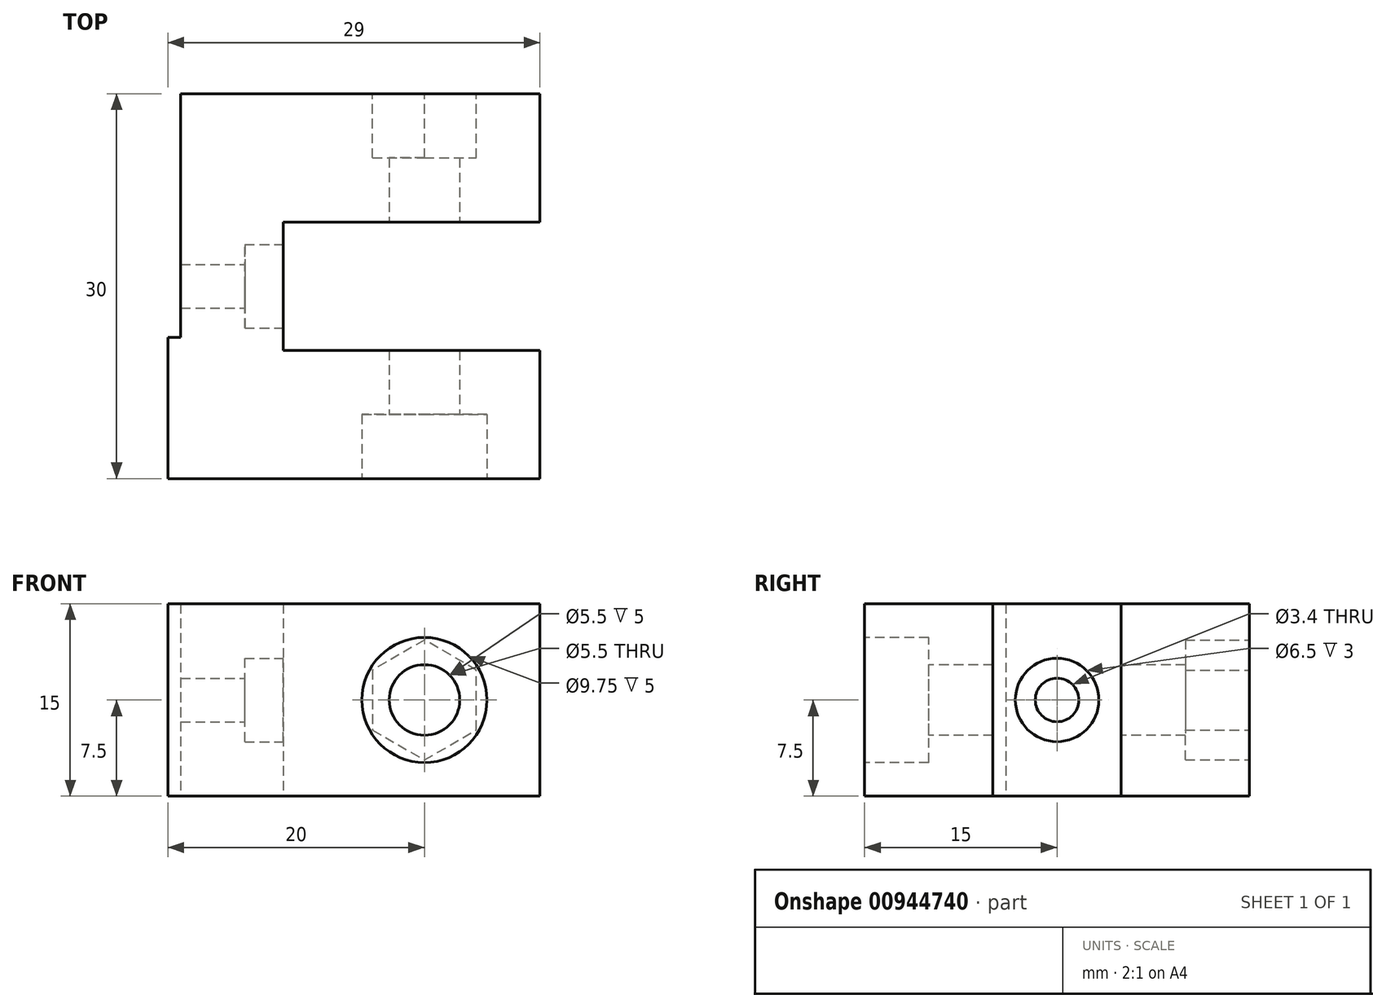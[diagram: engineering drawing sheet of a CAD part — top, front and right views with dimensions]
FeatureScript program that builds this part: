
annotation { "Feature Type Name" : "Feature", "Feature Type Description" : "" }
export const myFeature = defineFeature(function(context is Context, id is Id, definition is map)
    precondition{}
    {
        {
            var Q0;
            Q0=qCreatedBy(makeId("Top.planeOp"),FACE);
            var sketch = newSketch(context, id + "F0", { "sketchPlane" : qUnion([Q0])});
            skLineSegment(sketch, "E0", {"start": v(0, 0) * mm, "end": v(0, 15) * mm});
            skLineSegment(sketch, "E1", {"start": v(0, 15) * mm, "end": v(28, 15) * mm});
            skLineSegment(sketch, "E2", {"start": v(28, 15) * mm, "end": v(28, 5) * mm});
            skLineSegment(sketch, "E3", {"start": v(28, 5) * mm, "end": v(8, 5) * mm});
            skLineSegment(sketch, "E4", {"start": v(8, 5) * mm, "end": v(8, 0) * mm});
            skLineSegment(sketch, "E5", {"start": v(8, 0) * mm, "end": v(0, 0) * mm, "construction": true});
            skPoint(sketch, "E6", {"position": v(19, 15) * mm});
            skLineSegment(sketch, "E7.MirrorCS", {"start": v(8, -5) * mm, "end": v(8, 0) * mm});
            skLineSegment(sketch, "E8.MirrorCS", {"start": v(28, -5) * mm, "end": v(8, -5) * mm});
            skLineSegment(sketch, "E9.MirrorCS", {"start": v(28, -15) * mm, "end": v(28, -5) * mm});
            skLineSegment(sketch, "E10.MirrorCS", {"start": v(-1, -15) * mm, "end": v(28, -15) * mm});
            skLineSegment(sketch, "E11", {"start": v(0, -4) * mm, "end": v(-1, -4) * mm});
            skLineSegment(sketch, "E12", {"start": v(-1, -4) * mm, "end": v(-1, -15) * mm});
            skLineSegment(sketch, "E13", {"start": v(0, 0) * mm, "end": v(0, -4) * mm});
            skSolve(sketch);
        }
        {
            var Q0;
            Q0 = qSketchRegion(id + "F0", true);
            extrude(context, id + "F1", {"entities" : qUnion([Q0]), "depth" : 15 * mm, "offsetDistance" : 25 * mm});
        }
        {
            var Q0;
            Q0=makeQuery(id+"F1.opExtrude","SWEPT_FACE",FACE,{"disambiguationData":[OSD([sQuery(id+"F0.wireOp",EDGE,"E10.MirrorCS")])]});
            var sketch = newSketch(context, id + "F2", { "sketchPlane" : qUnion([Q0])});
            skLineSegment(sketch, "E14", {"start": v(28, 7.5) * mm, "end": v(19, 7.5) * mm, "construction": true});
            skLineSegment(sketch, "E15", {"start": v(19, 0) * mm, "end": v(19, 7.5) * mm, "construction": true});
            skSolve(sketch);
        }
        {
            var Q0;
            Q0=sQuery(id+"F2.wireOp",VERTEX,"E14.end");
            var Q1;
            Q1=makeQuery(id+"F1.opExtrude","SWEPT_BODY",BODY,{"disambiguationData":[OSD([sQuery(id+"F0.wireOp",EDGE,"E0"),sQuery(id+"F0.wireOp",EDGE,"E1"),sQuery(id+"F0.wireOp",EDGE,"E2"),sQuery(id+"F0.wireOp",EDGE,"E3"),sQuery(id+"F0.wireOp",EDGE,"E4"),sQuery(id+"F0.wireOp",EDGE,"E7.MirrorCS"),sQuery(id+"F0.wireOp",EDGE,"E8.MirrorCS"),sQuery(id+"F0.wireOp",EDGE,"E9.MirrorCS"),sQuery(id+"F0.wireOp",EDGE,"E10.MirrorCS"),sQuery(id+"F0.wireOp",EDGE,"E11"),sQuery(id+"F0.wireOp",EDGE,"E12"),sQuery(id+"F0.wireOp",EDGE,"E13")])]});
            hole(context, id + "F3", {"style" : HoleStyle.C_BORE, "endStyle" : HoleEndStyle.THROUGH, "standardTappedOrClearance" : lookupTablePath({ "fit" : "Normal", "standard" : "ISO", "size" : "M5", "type" : "Clearance" }), "standardBlindInLast" : lookupTablePath({ "fit" : "Normal", "standard" : "ISO", "engagement" : "75%", "pitch" : "0.8 mm", "size" : "M5", "type" : "Clearance & tapped" }), "holeDiameter" : 5.5 * mm, "cBoreDiameter" : 9.75 * mm, "cBoreDepth" : 5 * mm, "majorDiameter" : 5 * mm, "isTappedThrough" : true, "tappedDepth" : 12 * mm, "tapClearance" : 3, "startFromSketch" : true, "locations" : qUnion([Q0]), "scope" : qUnion([Q1])});
        }
        {
            var Q0;
            Q0=makeQuery(id+"F1.opExtrude","SWEPT_FACE",FACE,{"disambiguationData":[OSD([sQuery(id+"F0.wireOp",EDGE,"E4"),sQuery(id+"F0.wireOp",EDGE,"E7.MirrorCS")])]});
            var sketch = newSketch(context, id + "F4", { "sketchPlane" : qUnion([Q0])});
            skLineSegment(sketch, "E16", {"start": v(-5, 7.5) * mm, "end": v(0, 7.5) * mm, "construction": true});
            skLineSegment(sketch, "E17", {"start": v(0, 7.5) * mm, "end": v(0, 0) * mm, "construction": true});
            skSolve(sketch);
        }
        {
            var Q0;
            Q0=sQuery(id+"F4.wireOp",VERTEX,"E16.end");
            var Q1;
            Q1=makeQuery(id+"F1.opExtrude","SWEPT_BODY",BODY,{"disambiguationData":[OSD([sQuery(id+"F0.wireOp",EDGE,"E0"),sQuery(id+"F0.wireOp",EDGE,"E1"),sQuery(id+"F0.wireOp",EDGE,"E2"),sQuery(id+"F0.wireOp",EDGE,"E3"),sQuery(id+"F0.wireOp",EDGE,"E4"),sQuery(id+"F0.wireOp",EDGE,"E7.MirrorCS"),sQuery(id+"F0.wireOp",EDGE,"E8.MirrorCS"),sQuery(id+"F0.wireOp",EDGE,"E9.MirrorCS"),sQuery(id+"F0.wireOp",EDGE,"E10.MirrorCS"),sQuery(id+"F0.wireOp",EDGE,"E11"),sQuery(id+"F0.wireOp",EDGE,"E12"),sQuery(id+"F0.wireOp",EDGE,"E13")])]});
            hole(context, id + "F5", {"style" : HoleStyle.C_BORE, "endStyle" : HoleEndStyle.THROUGH, "standardTappedOrClearance" : lookupTablePath({ "fit" : "Normal", "standard" : "ISO", "size" : "M3", "type" : "Clearance" }), "standardBlindInLast" : lookupTablePath({ "fit" : "Normal", "standard" : "ISO", "engagement" : "75%", "pitch" : "0.5 mm", "size" : "M3", "type" : "Clearance & tapped" }), "holeDiameter" : 3.4 * mm, "cBoreDiameter" : 6.5 * mm, "cBoreDepth" : 3 * mm, "majorDiameter" : 5 * mm, "isTappedThrough" : true, "tappedDepth" : 12 * mm, "tapClearance" : 3, "startFromSketch" : true, "locations" : qUnion([Q0]), "scope" : qUnion([Q1])});
        }
        {
            var Q0;
            Q0=makeQuery(id+"F1.opExtrude","SWEPT_FACE",FACE,{"disambiguationData":[OSD([sQuery(id+"F0.wireOp",EDGE,"E1")])]});
            var sketch = newSketch(context, id + "F6", { "sketchPlane" : qUnion([Q0])});
            skCircle(sketch, "E18.cCircle", {"center": v(-19, 7.5) * mm, "radius": 4.05 * mm, "construction": true});
            skLineSegment(sketch, "E18.0", {"start": v(-19, 2.82) * mm, "end": v(-23.05, 5.16) * mm});
            skLineSegment(sketch, "E18.1", {"start": v(-23.05, 5.16) * mm, "end": v(-23.05, 9.84) * mm});
            skLineSegment(sketch, "E18.2", {"start": v(-23.05, 9.84) * mm, "end": v(-19, 12.18) * mm});
            skLineSegment(sketch, "E18.3", {"start": v(-19, 12.18) * mm, "end": v(-14.95, 9.84) * mm});
            skLineSegment(sketch, "E18.4", {"start": v(-14.95, 9.84) * mm, "end": v(-14.95, 5.16) * mm});
            skLineSegment(sketch, "E18.5", {"start": v(-14.95, 5.16) * mm, "end": v(-19, 2.82) * mm});
            skPoint(sketch, "E18.0.midPoint", {"position": v(-21.03, 4) * mm});
            skSolve(sketch);
        }
        {
            var Q0;
            Q0 = qSketchRegion(id + "F6", true);
            extrude(context, id + "F7", {"entities" : qUnion([Q0]), "operationType" : NewBodyOperationType.REMOVE, "oppositeDirection" : true, "depth" : 5 * mm, "offsetDistance" : 25 * mm});
        }
    });
